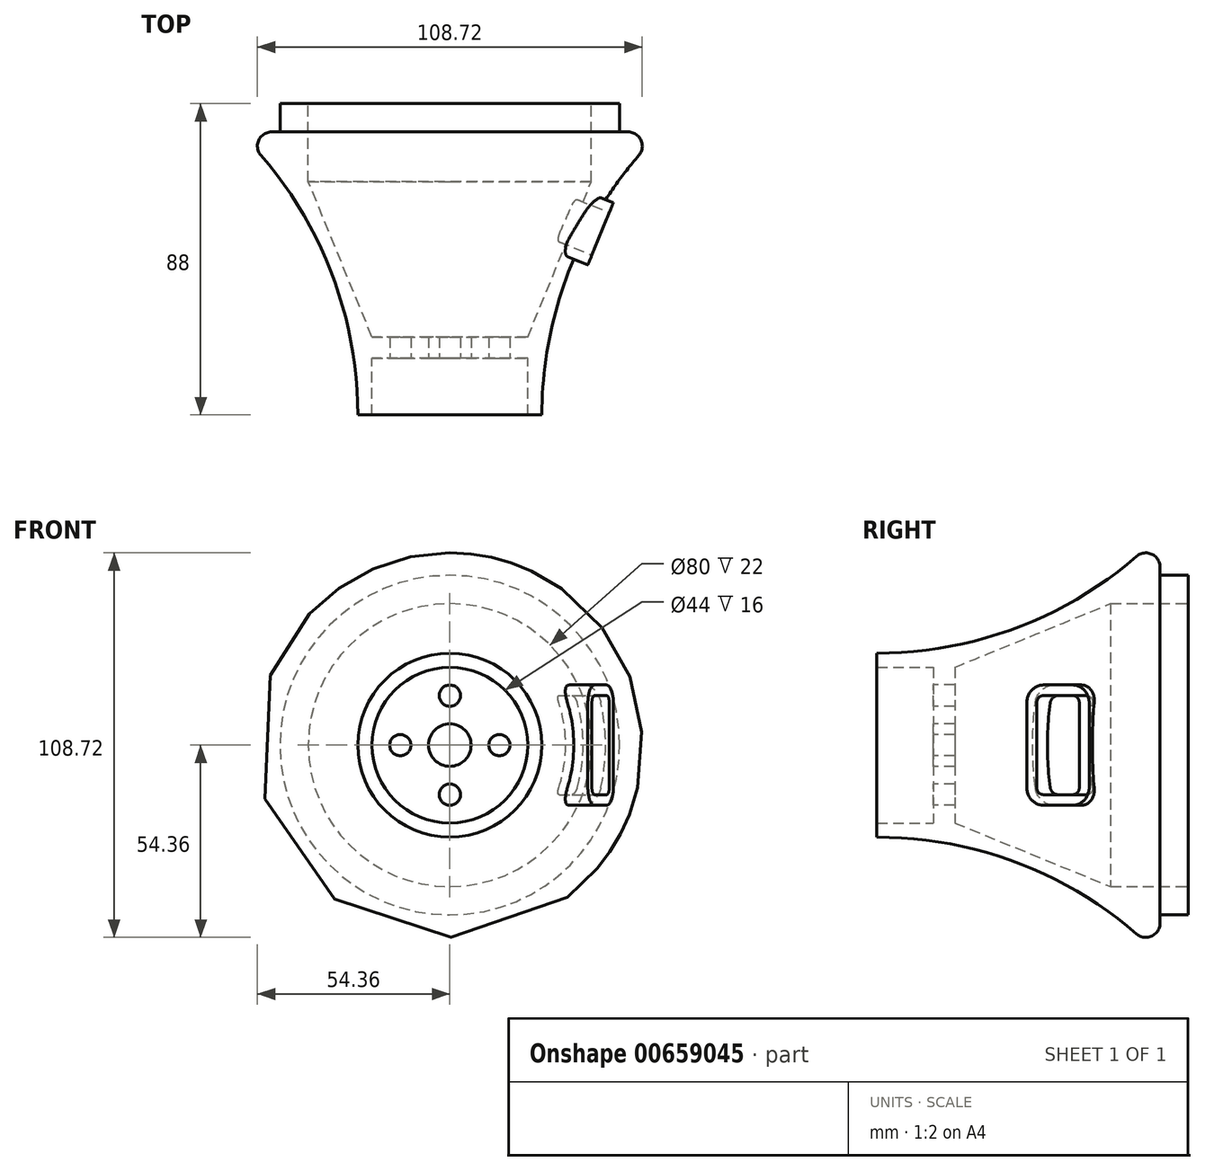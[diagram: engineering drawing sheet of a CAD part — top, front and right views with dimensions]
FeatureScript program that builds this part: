
annotation { "Feature Type Name" : "Feature", "Feature Type Description" : "" }
export const myFeature = defineFeature(function(context is Context, id is Id, definition is map)
    precondition{}
    {
        {
            var Q0;
            Q0=qCreatedBy(makeId("Top.planeOp"),FACE);
            var sketch = newSketch(context, id + "F0", { "sketchPlane" : qUnion([Q0])});
            skLineSegment(sketch, "E0", {"start": v(0, 62.35) * mm, "end": v(0, -50.5) * mm, "construction": true});
            skLineSegment(sketch, "E1.0", {"start": v(6, 62.35) * mm, "end": v(6, -50.5) * mm, "construction": true});
            skLineSegment(sketch, "E2.0", {"start": v(22, 62.35) * mm, "end": v(22, -50.5) * mm, "construction": true});
            skLineSegment(sketch, "E3.0", {"start": v(26, 62.35) * mm, "end": v(26, -50.5) * mm, "construction": true});
            skLineSegment(sketch, "E4.0", {"start": v(40, 88) * mm, "end": v(40, -50.5) * mm, "construction": true});
            skLineSegment(sketch, "E5", {"start": v(0, 0) * mm, "end": v(138, 0) * mm, "construction": true});
            skLineSegment(sketch, "E6.0", {"start": v(0, 16) * mm, "end": v(62.6, 16) * mm, "construction": true});
            skLineSegment(sketch, "E7.0", {"start": v(0, 22) * mm, "end": v(62.6, 22) * mm, "construction": true});
            skLineSegment(sketch, "E8.0", {"start": v(48, 88) * mm, "end": v(48, -50.5) * mm, "construction": true});
            skLineSegment(sketch, "E9.0", {"start": v(138, 62.35) * mm, "end": v(138, -50.5) * mm, "construction": true});
            skArc(sketch, "E10", {"start": v(53.39, 73.38) * mm, "mid": v(33.07, 39.16) * mm, "end": v(26, 0) * mm});
            skLineSegment(sketch, "E11.0", {"start": v(0, 88) * mm, "end": v(138, 88) * mm, "construction": true});
            skLineSegment(sketch, "E12.0", {"start": v(0, 80) * mm, "end": v(138, 80) * mm, "construction": true});
            skLineSegment(sketch, "E13.0", {"start": v(0, 66) * mm, "end": v(138, 66) * mm, "construction": true});
            skLineSegment(sketch, "E14.0", {"start": v(0, 63) * mm, "end": v(138, 63) * mm, "construction": true});
            skLineSegment(sketch, "E15", {"start": v(40, 66) * mm, "end": v(40, 88) * mm});
            skLineSegment(sketch, "E16", {"start": v(48, 88) * mm, "end": v(48, 80) * mm});
            skLineSegment(sketch, "E17", {"start": v(22, 0) * mm, "end": v(22, 16) * mm});
            skLineSegment(sketch, "E18", {"start": v(22, 16) * mm, "end": v(0, 16) * mm});
            skLineSegment(sketch, "E19", {"start": v(0, 22) * mm, "end": v(22, 22) * mm});
            skLineSegment(sketch, "E20", {"start": v(22, 22) * mm, "end": v(40, 66) * mm});
            skLineSegment(sketch, "E21", {"start": v(22, 0) * mm, "end": v(26, 0) * mm});
            skLineSegment(sketch, "E22", {"start": v(48, 80) * mm, "end": v(50.36, 80) * mm});
            skPoint(sketch, "E23.visualSharp", {"position": v(59.62, 80) * mm});
            skArc(sketch, "E23.filletArc", {"start": v(53.39, 73.38) * mm, "mid": v(54, 77.66) * mm, "end": v(50.36, 80) * mm});
            skLineSegment(sketch, "E24", {"start": v(40, 88) * mm, "end": v(48, 88) * mm});
            skLineSegment(sketch, "E25", {"start": v(0, 22) * mm, "end": v(0, 16) * mm});
            skPoint(sketch, "E26", {"position": v(38.77, 63) * mm});
            skSolve(sketch);
        }
        {
            var Q0;
            Q0=makeQuery(id+"F0.imprint","IMPRINT",FACE,{"disambiguationData":[TD([[makeQuery(id+"F0.imprint","IMPRINT",EDGE,{"derivedFrom":sQuery(id+"F0.wireOp",EDGE,"E10")}),-1.0]])]});
            var Q1;
            Q1=sQuery(id+"F0.wireOp",EDGE,"E0");
            revolve(context, id + "F1", {"entities" : qUnion([Q0]), "axis" : qUnion([Q1]), "revolveType" : RevolveType.FULL});
        }
        {
            var Q0;
            Q0=makeQuery(id+"F1.opRevolve","SWEPT_FACE",FACE,{"disambiguationData":[OSD([sQuery(id+"F0.wireOp",EDGE,"E18")])]});
            var sketch = newSketch(context, id + "F2", { "sketchPlane" : qUnion([Q0])});
            skCircle(sketch, "E27", {"center": v(0, 0) * mm, "radius": 6 * mm});
            skCircle(sketch, "E28", {"center": v(0, 0) * mm, "radius": 14 * mm, "construction": true});
            skLineSegment(sketch, "E29", {"start": v(-14, 0) * mm, "end": v(14, 0) * mm, "construction": true});
            skLineSegment(sketch, "E30", {"start": v(0, 14) * mm, "end": v(0, -14) * mm, "construction": true});
            skCircle(sketch, "E31", {"center": v(0, 14) * mm, "radius": 3 * mm});
            skCircle(sketch, "E32", {"center": v(-14, 0) * mm, "radius": 3 * mm});
            skCircle(sketch, "E33", {"center": v(0, -14) * mm, "radius": 3 * mm});
            skCircle(sketch, "E34", {"center": v(14, 0) * mm, "radius": 3 * mm});
            skSolve(sketch);
        }
        {
            var Q0;
            Q0=makeQuery(id+"F2.imprint","IMPRINT",FACE,{"disambiguationData":[TD([[makeQuery(id+"F2.imprint","IMPRINT",EDGE,{"derivedFrom":sQuery(id+"F2.wireOp",EDGE,"E27")}),1.0]])]});
            extrude(context, id + "F3", {"entities" : qUnion([Q0]), "operationType" : NewBodyOperationType.REMOVE, "endBound" : BoundingType.THROUGH_ALL, "oppositeDirection" : true, "depth" : 25 * mm, "offsetDistance" : 25 * mm});
        }
        {
            var Q0;
            Q0=makeQuery(id+"F2.imprint","IMPRINT",FACE,{"disambiguationData":[TD([[makeQuery(id+"F2.imprint","IMPRINT",EDGE,{"derivedFrom":sQuery(id+"F2.wireOp",EDGE,"E32")}),1.0]])]});
            var Q1;
            Q1=makeQuery(id+"F2.imprint","IMPRINT",FACE,{"disambiguationData":[TD([[makeQuery(id+"F2.imprint","IMPRINT",EDGE,{"derivedFrom":sQuery(id+"F2.wireOp",EDGE,"E31")}),1.0]])]});
            var Q2;
            Q2=makeQuery(id+"F2.imprint","IMPRINT",FACE,{"disambiguationData":[TD([[makeQuery(id+"F2.imprint","IMPRINT",EDGE,{"derivedFrom":sQuery(id+"F2.wireOp",EDGE,"E34")}),1.0]])]});
            var Q3;
            Q3=makeQuery(id+"F2.imprint","IMPRINT",FACE,{"disambiguationData":[TD([[makeQuery(id+"F2.imprint","IMPRINT",EDGE,{"derivedFrom":sQuery(id+"F2.wireOp",EDGE,"E33")}),1.0]])]});
            extrude(context, id + "F4", {"entities" : qUnion([Q0, Q1, Q2, Q3]), "operationType" : NewBodyOperationType.REMOVE, "endBound" : BoundingType.THROUGH_ALL, "oppositeDirection" : true, "depth" : 25 * mm, "offsetDistance" : 25 * mm});
        }
        {
            var Q0;
            Q0=sQuery(id+"F0.wireOp",EDGE,"E20");
            cPlane(context, id + "F5", {"entities" : qUnion([Q0]), "cplaneType" : CPlaneType.LINE_ANGLE, "offset" : 25 * mm, "angle" : 90 * degree, "width" : 150 * mm, "height" : 150 * mm});
        }
        {
            var Q0;
            Q0=qCreatedBy(id+"F5.planeOp",FACE);
            var sketch = newSketch(context, id + "F6", { "sketchPlane" : qUnion([Q0])});
            skPoint(sketch, "E35.0", {"position": v(73, 0) * mm});
            skLineSegment(sketch, "E36", {"start": v(73, 0) * mm, "end": v(63.5, 0) * mm, "construction": true});
            skLineSegment(sketch, "E37.bottom", {"start": v(68, 17) * mm, "end": v(59, 17) * mm});
            skLineSegment(sketch, "E37.top", {"start": v(68, -17) * mm, "end": v(59, -17) * mm});
            skLineSegment(sketch, "E37.left", {"start": v(73, 12) * mm, "end": v(73, -12) * mm});
            skLineSegment(sketch, "E37.right", {"start": v(54, 12) * mm, "end": v(54, -12) * mm});
            skPoint(sketch, "E37.middle", {"position": v(63.5, 0) * mm});
            skLineSegment(sketch, "E38.bottom", {"start": v(68, 14) * mm, "end": v(59, 14) * mm});
            skLineSegment(sketch, "E38.top", {"start": v(68, -14) * mm, "end": v(59, -14) * mm});
            skLineSegment(sketch, "E38.left", {"start": v(70, 12) * mm, "end": v(70, -12) * mm});
            skLineSegment(sketch, "E38.right", {"start": v(57, 12) * mm, "end": v(57, -12) * mm});
            skPoint(sketch, "E39.visualSharp", {"position": v(54, 17) * mm});
            skArc(sketch, "E39.filletArc", {"start": v(59, 17) * mm, "mid": v(55.45, 15.54) * mm, "end": v(54, 12) * mm});
            skPoint(sketch, "E40.visualSharp", {"position": v(54, -17) * mm});
            skArc(sketch, "E40.filletArc", {"start": v(54, -12) * mm, "mid": v(55.45, -15.54) * mm, "end": v(59, -17) * mm});
            skPoint(sketch, "E41.visualSharp", {"position": v(73, -17) * mm});
            skArc(sketch, "E41.filletArc", {"start": v(68, -17) * mm, "mid": v(71.53, -15.54) * mm, "end": v(73, -12) * mm});
            skPoint(sketch, "E42.visualSharp", {"position": v(73, 17) * mm});
            skArc(sketch, "E42.filletArc", {"start": v(73, 12) * mm, "mid": v(71.53, 15.54) * mm, "end": v(68, 17) * mm});
            skPoint(sketch, "E43.visualSharp", {"position": v(70, 14) * mm});
            skArc(sketch, "E43.filletArc", {"start": v(70, 12) * mm, "mid": v(69.4, 13.41) * mm, "end": v(68, 14) * mm});
            skPoint(sketch, "E44.visualSharp", {"position": v(57, 14) * mm});
            skArc(sketch, "E44.filletArc", {"start": v(59, 14) * mm, "mid": v(57.58, 13.41) * mm, "end": v(57, 12) * mm});
            skPoint(sketch, "E45.visualSharp", {"position": v(57, -14) * mm});
            skArc(sketch, "E45.filletArc", {"start": v(57, -12) * mm, "mid": v(57.58, -13.41) * mm, "end": v(59, -14) * mm});
            skPoint(sketch, "E46.visualSharp", {"position": v(70, -14) * mm});
            skArc(sketch, "E46.filletArc", {"start": v(68, -14) * mm, "mid": v(69.4, -13.41) * mm, "end": v(70, -12) * mm});
            skSolve(sketch);
        }
        {
            var Q0;
            Q0=makeQuery(id+"F6.imprint","IMPRINT",FACE,{"disambiguationData":[TD([[makeQuery(id+"F6.imprint","IMPRINT",EDGE,{"derivedFrom":sQuery(id+"F6.wireOp",EDGE,"E38.bottom")}),1.0]])]});
            extrude(context, id + "F7", {"entities" : qUnion([Q0]), "operationType" : NewBodyOperationType.REMOVE, "endBound" : BoundingType.SYMMETRIC, "oppositeDirection" : true, "depth" : 25 * mm, "offsetDistance" : 25 * mm});
        }
        {
            var Q0;
            Q0=makeQuery(id+"F6.imprint","IMPRINT",FACE,{"disambiguationData":[TD([[makeQuery(id+"F6.imprint","IMPRINT",EDGE,{"derivedFrom":sQuery(id+"F6.wireOp",EDGE,"E37.bottom")}),1.0]])]});
            extrude(context, id + "F8", {"entities" : qUnion([Q0]), "operationType" : NewBodyOperationType.ADD, "depth" : 8 * mm, "offsetDistance" : 25 * mm});
        }
    });
